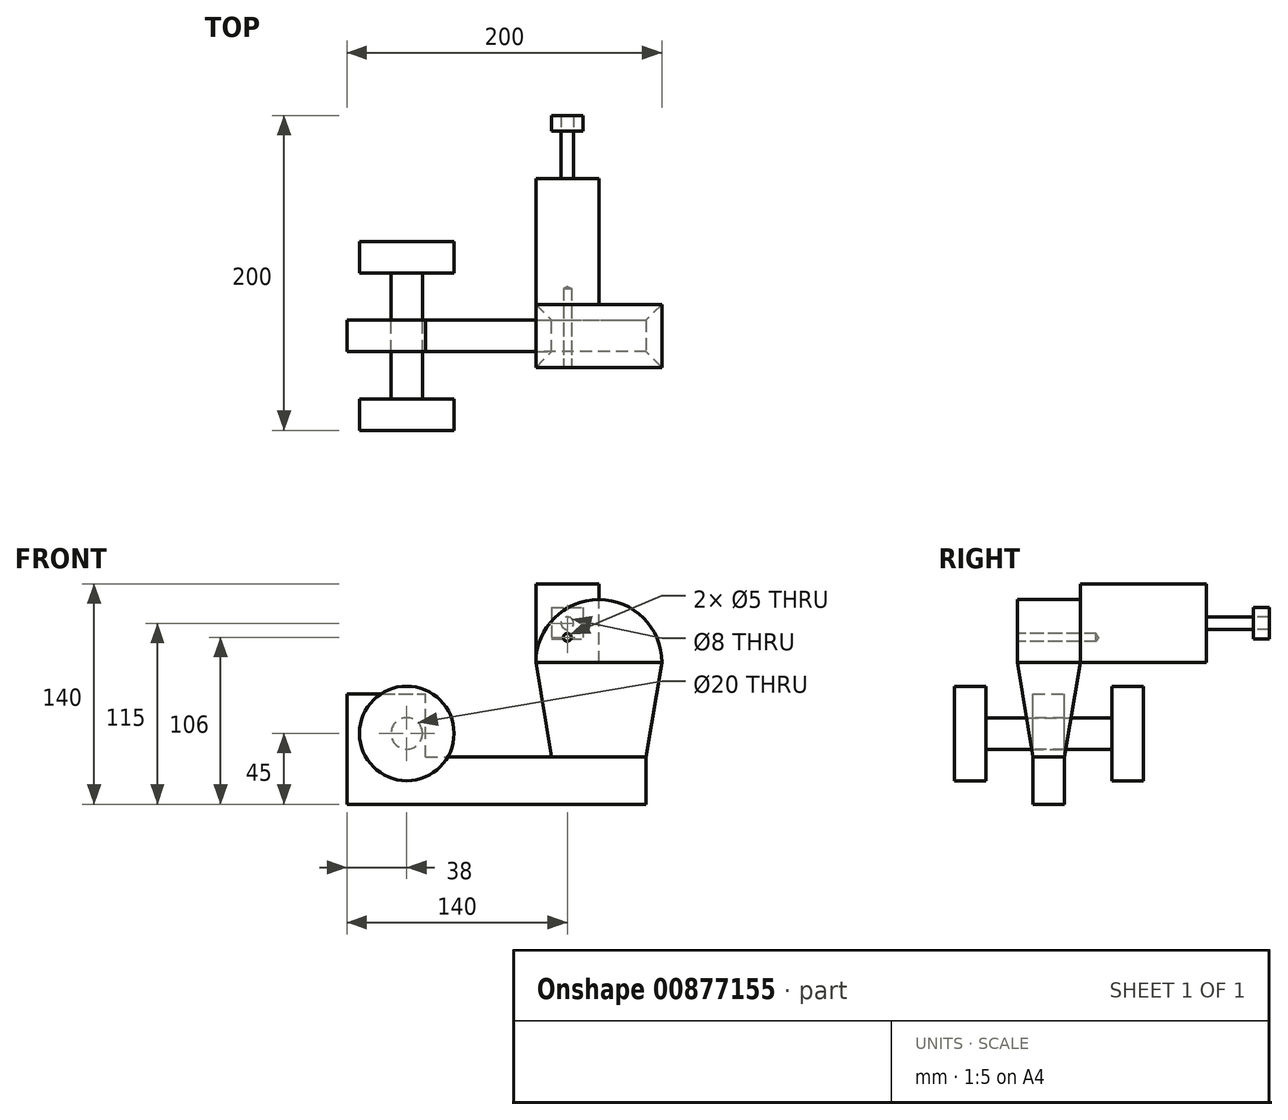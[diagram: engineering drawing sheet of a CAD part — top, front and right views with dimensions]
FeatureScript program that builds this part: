
annotation { "Feature Type Name" : "Feature", "Feature Type Description" : "" }
export const myFeature = defineFeature(function(context is Context, id is Id, definition is map)
    precondition{}
    {
        {
            var Q0;
            Q0=qCreatedBy(makeId("Front.planeOp"),FACE);
            var sketch = newSketch(context, id + "F0", { "sketchPlane" : qUnion([Q0])});
            skLineSegment(sketch, "E0.bottom", {"start": v(0, 0) * mm, "end": v(-40, 0) * mm});
            skLineSegment(sketch, "E0.top", {"start": v(0, 50) * mm, "end": v(-40, 50) * mm});
            skLineSegment(sketch, "E0.left", {"start": v(0, 0) * mm, "end": v(0, 50) * mm});
            skLineSegment(sketch, "E0.right", {"start": v(-40, 0) * mm, "end": v(-40, 50) * mm});
            skSolve(sketch);
        }
        {
            var Q0;
            Q0 = qSketchRegion(id + "F0", true);
            extrude(context, id + "F1", {"entities" : qUnion([Q0]), "oppositeDirection" : true, "depth" : 80 * mm, "offsetDistance" : 25 * mm});
        }
        {
            var Q0;
            Q0=qCreatedBy(makeId("Front.planeOp"),FACE);
            var sketch = newSketch(context, id + "F2", { "sketchPlane" : qUnion([Q0])});
            skArc(sketch, "E1", {"start": v(-40, 0) * mm, "mid": v(-28.28, 28.28) * mm, "end": v(0, 40) * mm});
            skArc(sketch, "E2.MirrorCS", {"start": v(40, 0) * mm, "mid": v(28.28, 28.28) * mm, "end": v(0, 40) * mm});
            skLineSegment(sketch, "E3", {"start": v(40, 0) * mm, "end": v(-40, 0) * mm});
            skSolve(sketch);
        }
        {
            var Q0;
            Q0 = qSketchRegion(id + "F2", true);
            extrude(context, id + "F3", {"entities" : qUnion([Q0]), "depth" : 40 * mm, "offsetDistance" : 25 * mm});
        }
        {
            var Q0;
            Q0=qCreatedBy(makeId("Top.planeOp"),FACE);
            cPlane(context, id + "F4", {"entities" : qUnion([Q0]), "cplaneType" : CPlaneType.OFFSET, "offset" : 60 * mm, "oppositeDirection" : true, "width" : 150 * mm, "height" : 150 * mm});
        }
        {
            var Q0;
            Q0=qCreatedBy(id+"F4.planeOp",FACE);
            var sketch = newSketch(context, id + "F5", { "sketchPlane" : qUnion([Q0])});
            skLineSegment(sketch, "E4.0", {"start": v(-30, -10) * mm, "end": v(30, -10) * mm});
            skLineSegment(sketch, "E4.1", {"start": v(-30, -30) * mm, "end": v(-30, -10) * mm});
            skLineSegment(sketch, "E4.2", {"start": v(30, -30) * mm, "end": v(-30, -30) * mm});
            skLineSegment(sketch, "E4.3", {"start": v(30, -10) * mm, "end": v(30, -30) * mm});
            skSolve(sketch);
        }
        {
            var Q0;
            Q0 = qSketchRegion(id + "F5", true);
            extrude(context, id + "F6", {"entities" : qUnion([Q0]), "oppositeDirection" : true, "depth" : 30 * mm, "offsetDistance" : 25 * mm});
        }
        {
            var Q0;
            Q0=makeQuery(id+"F3.opExtrude","SWEPT_FACE",FACE,{"disambiguationData":[OSD([sQuery(id+"F2.wireOp",EDGE,"E3")])]});
            var Q1;
            Q1=makeQuery(id+"F6.opExtrude","CAP_FACE",FACE,{"disambiguationData":[OSD([sQuery(id+"F5.wireOp",EDGE,"E4.0"),sQuery(id+"F5.wireOp",EDGE,"E4.1"),sQuery(id+"F5.wireOp",EDGE,"E4.2"),sQuery(id+"F5.wireOp",EDGE,"E4.3")])],"isStart":true});
            loft(context, id + "F7", {"sheetProfilesArray" : [{ "sheetProfileEntities" : qUnion([Q0]) }, { "sheetProfileEntities" : qUnion([Q1]) }]});
        }
        {
            var Q0;
            Q0=makeQuery(id+"F6.opExtrude","SWEPT_FACE",FACE,{"disambiguationData":[OSD([sQuery(id+"F5.wireOp",EDGE,"E4.1")])]});
            extrude(context, id + "F8", {"entities" : qUnion([Q0]), "operationType" : NewBodyOperationType.ADD, "depth" : 80 * mm, "offsetDistance" : 25 * mm});
        }
        {
            var Q0;
            Q0=makeQuery(id+"F8.opExtrude","CAP_FACE",FACE,{"disambiguationData":[OSD([sQuery(id+"F5.wireOp",EDGE,"E4.1")])],"isStart":false});
            extrude(context, id + "F9", {"entities" : qUnion([Q0]), "depth" : 50 * mm, "offsetDistance" : 25 * mm});
        }
        {
            var Q0;
            {var subQ0=sQuery(id+"F5.wireOp",EDGE,"E4.1");Q0=makeQuery(id+"F9.opExtrude","SWEPT_FACE",FACE,{"disambiguationData":[OSD([subQ0]),TDD([makeQuery(id+"F8.opExtrude","CAP_EDGE",EDGE,{"disambiguationData":[OSD([subQ0]),TDD([makeQuery(id+"F6.opExtrude","CAP_EDGE",EDGE,{"disambiguationData":[OSD([subQ0])],"isStart":true})])],"isStart":false})])]});}
            extrude(context, id + "F10", {"entities" : qUnion([Q0]), "operationType" : NewBodyOperationType.ADD, "depth" : 40 * mm, "offsetDistance" : 25 * mm});
        }
        {
            var Q0;
            {var subQ0=sQuery(id+"F5.wireOp",EDGE,"E4.2");var subQ1=sQuery(id+"F5.wireOp",EDGE,"E4.1");Q0=makeQuery(id+"F10.boolean.opBoolean","MERGE",FACE,{"derivedFrom":[makeQuery(id+"F9.opExtrude","SWEPT_FACE",FACE,{"disambiguationData":[OSD([subQ1,subQ0])]}),makeQuery(id+"F10.opExtrude","SWEPT_FACE",FACE,{"disambiguationData":[OSD([subQ1,subQ0])]})]});}
            var sketch = newSketch(context, id + "F11", { "sketchPlane" : qUnion([Q0])});
            skCircle(sketch, "E5", {"center": v(-122, -45) * mm, "radius": 10 * mm});
            skSolve(sketch);
        }
        {
            var Q0;
            Q0 = qSketchRegion(id + "F11", true);
            extrude(context, id + "F12", {"entities" : qUnion([Q0]), "operationType" : NewBodyOperationType.REMOVE, "oppositeDirection" : true, "depth" : 20 * mm, "offsetDistance" : 25 * mm});
        }
        {
            var Q0;
            Q0=qCreatedBy(makeId("Front.planeOp"),FACE);
            cPlane(context, id + "F13", {"entities" : qUnion([Q0]), "cplaneType" : CPlaneType.OFFSET, "offset" : 20 * mm, "width" : 150 * mm, "height" : 150 * mm});
        }
        {
            var Q0;
            Q0=qCreatedBy(id+"F13.planeOp",FACE);
            var sketch = newSketch(context, id + "F14", { "sketchPlane" : qUnion([Q0])});
            skCircle(sketch, "E6", {"center": v(-122, -45) * mm, "radius": 10 * mm});
            skSolve(sketch);
        }
        {
            var Q0;
            Q0 = qSketchRegion(id + "F14", true);
            extrude(context, id + "F15", {"entities" : qUnion([Q0]), "endBound" : BoundingType.SYMMETRIC, "depth" : 80 * mm, "offsetDistance" : 25 * mm});
        }
        {
            var Q0;
            Q0=makeQuery(id+"F15.opExtrude","CAP_FACE",FACE,{"disambiguationData":[OSD([sQuery(id+"F14.wireOp",EDGE,"E6")])],"isStart":false});
            var sketch = newSketch(context, id + "F16", { "sketchPlane" : qUnion([Q0])});
            skCircle(sketch, "E7", {"center": v(-122, -45) * mm, "radius": 30 * mm});
            skSolve(sketch);
        }
        {
            var Q0;
            Q0 = qSketchRegion(id + "F16", true);
            extrude(context, id + "F17", {"entities" : qUnion([Q0]), "operationType" : NewBodyOperationType.ADD, "depth" : 20 * mm, "offsetDistance" : 25 * mm});
        }
        {
            var Q0;
            Q0=makeQuery(id+"F15.opExtrude","CAP_FACE",FACE,{"disambiguationData":[OSD([sQuery(id+"F14.wireOp",EDGE,"E6")])],"isStart":true});
            var sketch = newSketch(context, id + "F18", { "sketchPlane" : qUnion([Q0])});
            skCircle(sketch, "E8", {"center": v(122, -45) * mm, "radius": 30 * mm});
            skSolve(sketch);
        }
        {
            var Q0;
            Q0 = qSketchRegion(id + "F18", true);
            extrude(context, id + "F19", {"entities" : qUnion([Q0]), "operationType" : NewBodyOperationType.ADD, "depth" : 20 * mm, "offsetDistance" : 25 * mm});
        }
        {
            var Q0;
            Q0=makeQuery(id+"F3.opExtrude","CAP_FACE",FACE,{"disambiguationData":[OSD([sQuery(id+"F2.wireOp",EDGE,"E1"),sQuery(id+"F2.wireOp",EDGE,"E2.MirrorCS"),sQuery(id+"F2.wireOp",EDGE,"E3")])],"isStart":false});
            var sketch = newSketch(context, id + "F20", { "sketchPlane" : qUnion([Q0])});
            skPoint(sketch, "E9", {"position": v(-20, 16) * mm});
            skSolve(sketch);
        }
        {
            var Q0;
            Q0=sQuery(id+"F20.wireOp",VERTEX,"E9");
            var Q1;
            Q1=makeQuery(id+"F1.opExtrude","SWEPT_BODY",BODY,{"disambiguationData":[OSD([sQuery(id+"F0.wireOp",EDGE,"E0.bottom"),sQuery(id+"F0.wireOp",EDGE,"E0.top"),sQuery(id+"F0.wireOp",EDGE,"E0.left"),sQuery(id+"F0.wireOp",EDGE,"E0.right")])]});
            var Q2;
            Q2=makeQuery(id+"F3.opExtrude","SWEPT_BODY",BODY,{"disambiguationData":[OSD([sQuery(id+"F2.wireOp",EDGE,"E1"),sQuery(id+"F2.wireOp",EDGE,"E2.MirrorCS"),sQuery(id+"F2.wireOp",EDGE,"E3")])]});
            hole(context, id + "F21", {"style" : HoleStyle.SIMPLE, "endStyle" : HoleEndStyle.BLIND, "holeDiameter" : 5 * mm, "majorDiameter" : 5 * mm, "holeDepth" : 50 * mm, "isTappedThrough" : true, "tappedDepth" : 12 * mm, "tapClearance" : 3, "startFromSketch" : true, "locations" : qUnion([Q0]), "scope" : qUnion([Q1, Q2])});
        }
        {
            var Q0;
            Q0=makeQuery(id+"F3.opExtrude","CAP_FACE",FACE,{"disambiguationData":[OSD([sQuery(id+"F2.wireOp",EDGE,"E1"),sQuery(id+"F2.wireOp",EDGE,"E2.MirrorCS"),sQuery(id+"F2.wireOp",EDGE,"E3")])],"isStart":false});
            var sketch = newSketch(context, id + "F22", { "sketchPlane" : qUnion([Q0])});
            skCircle(sketch, "E10.0", {"center": v(-20, 16) * mm, "radius": 2.5 * mm});
            skSolve(sketch);
        }
        {
            var Q0;
            Q0 = qSketchRegion(id + "F22", true);
            var Q1;
            Q1=makeQuery(id+"F1.opExtrude","CAP_FACE",FACE,{"disambiguationData":[OSD([sQuery(id+"F0.wireOp",EDGE,"E0.bottom"),sQuery(id+"F0.wireOp",EDGE,"E0.top"),sQuery(id+"F0.wireOp",EDGE,"E0.left"),sQuery(id+"F0.wireOp",EDGE,"E0.right")])],"isStart":false});
            extrude(context, id + "F23", {"entities" : qUnion([Q0]), "endBound" : BoundingType.UP_TO_SURFACE, "oppositeDirection" : true, "depth" : 25 * mm, "endBoundEntityFace" : qUnion([Q1]), "offsetDistance" : 25 * mm});
        }
        {
            var Q0;
            Q0=makeQuery(id+"F3.opExtrude","SWEPT_BODY",BODY,{"disambiguationData":[OSD([sQuery(id+"F2.wireOp",EDGE,"E1"),sQuery(id+"F2.wireOp",EDGE,"E2.MirrorCS"),sQuery(id+"F2.wireOp",EDGE,"E3")])]});
            var Q1;
            Q1=makeQuery(id+"F1.opExtrude","SWEPT_BODY",BODY,{"disambiguationData":[OSD([sQuery(id+"F0.wireOp",EDGE,"E0.bottom"),sQuery(id+"F0.wireOp",EDGE,"E0.top"),sQuery(id+"F0.wireOp",EDGE,"E0.left"),sQuery(id+"F0.wireOp",EDGE,"E0.right")])]});
            var Q2;
            Q2=makeQuery(id+"F23.opExtrude","SWEPT_BODY",BODY,{"disambiguationData":[OSD([sQuery(id+"F22.wireOp",EDGE,"E10.0")])]});
            booleanBodies(context, id + "F24", {"operationType" : BooleanOperationType.SUBTRACTION, "tools" : qUnion([Q0, Q1]), "targets" : qUnion([Q2]), "keepTools" : true});
        }
        {
            var Q0;
            Q0=makeQuery(id+"F1.opExtrude","CAP_FACE",FACE,{"disambiguationData":[OSD([sQuery(id+"F0.wireOp",EDGE,"E0.bottom"),sQuery(id+"F0.wireOp",EDGE,"E0.top"),sQuery(id+"F0.wireOp",EDGE,"E0.left"),sQuery(id+"F0.wireOp",EDGE,"E0.right")])],"isStart":false});
            var sketch = newSketch(context, id + "F25", { "sketchPlane" : qUnion([Q0])});
            skCircle(sketch, "E11", {"center": v(20, 25) * mm, "radius": 4 * mm});
            skSolve(sketch);
        }
        {
            var Q0;
            Q0 = qSketchRegion(id + "F25", true);
            extrude(context, id + "F26", {"entities" : qUnion([Q0]), "operationType" : NewBodyOperationType.ADD, "depth" : 40 * mm, "offsetDistance" : 25 * mm});
        }
        {
            var Q0;
            Q0=makeQuery(id+"F26.opExtrude","CAP_FACE",FACE,{"disambiguationData":[OSD([sQuery(id+"F25.wireOp",EDGE,"E11")])],"isStart":false});
            var sketch = newSketch(context, id + "F27", { "sketchPlane" : qUnion([Q0])});
            skLineSegment(sketch, "E12.bottom", {"start": v(30, 35) * mm, "end": v(10, 35) * mm});
            skLineSegment(sketch, "E12.top", {"start": v(30, 15) * mm, "end": v(10, 15) * mm});
            skLineSegment(sketch, "E12.left", {"start": v(30, 35) * mm, "end": v(30, 15) * mm});
            skLineSegment(sketch, "E12.right", {"start": v(10, 35) * mm, "end": v(10, 15) * mm});
            skPoint(sketch, "E12.middle", {"position": v(20, 25) * mm});
            skSolve(sketch);
        }
        {
            var Q0;
            Q0 = qSketchRegion(id + "F27", true);
            extrude(context, id + "F28", {"entities" : qUnion([Q0]), "oppositeDirection" : true, "depth" : 10 * mm, "offsetDistance" : 25 * mm});
        }
        {
            var Q0;
            Q0=makeQuery(id+"F1.opExtrude","SWEPT_BODY",BODY,{"disambiguationData":[OSD([sQuery(id+"F0.wireOp",EDGE,"E0.bottom"),sQuery(id+"F0.wireOp",EDGE,"E0.top"),sQuery(id+"F0.wireOp",EDGE,"E0.left"),sQuery(id+"F0.wireOp",EDGE,"E0.right")])]});
            var Q1;
            Q1=makeQuery(id+"F28.opExtrude","SWEPT_BODY",BODY,{"disambiguationData":[OSD([sQuery(id+"F27.wireOp",EDGE,"E12.bottom"),sQuery(id+"F27.wireOp",EDGE,"E12.top"),sQuery(id+"F27.wireOp",EDGE,"E12.left"),sQuery(id+"F27.wireOp",EDGE,"E12.right")])]});
            booleanBodies(context, id + "F29", {"operationType" : BooleanOperationType.SUBTRACTION, "tools" : qUnion([Q0]), "targets" : qUnion([Q1]), "keepTools" : true});
        }
    });
